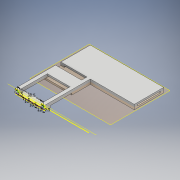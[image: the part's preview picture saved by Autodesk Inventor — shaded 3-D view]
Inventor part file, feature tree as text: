
AUTODESK INVENTOR PART (.ipt)
format: ipt  version: 2018 (Build 220112000, 112)  size: 287,232 bytes
history: native  units: mm
features: extrude x11, sketch x7, plane x3, other x2, mirror x2, projected_geometry x1
ambient origin geometry x8: Origin, YZ Plane, XZ Plane, XY Plane, X Axis, Y Axis, Z Axis, Center Point
bodies: Body1 (feature_tree)
feature tree (26):
  other  "Sólido1"
  sketch  "Boceto1"  dims[d7=5.0mm d9=2.5mm d10=0.0mm]
  extrude  "Extrusión1"  Depth=2.5mm TaperAngle=0.0deg
  extrude  "Extrusión2"  Depth=5.0mm
  plane  "Plano de trabajo3"
  mirror  "Simetría3"
  extrude  "Extrusión11"  Depth=5.0mm
  sketch  "Boceto7"  dims[d69=33.5mm d74=5.0mm]
  plane  "Plano de trabajo4"
  extrude  "Extrusión12"  Depth=5.0mm
  extrude  "Extrusión13"  Depth=8.0mm
  extrude  "Extrusión14"  Depth=42.4mm
  mirror  "Simetría4"
  extrude  "Extrusión15"  Depth=2.5mm TaperAngle=0.0deg
  sketch  "Boceto9"  dims[d77=70.0mm d78=8.0mm]
  other  "Eje de trabajo2"
  extrude  "Extrusión16"  TaperAngle=120.0deg  [1 undecoded]
  plane  "Plano de trabajo5"
  extrude  "Extrusión17"  Depth=5.0mm TaperAngle=0.0deg
  sketch  "Boceto11"  dims[d82=173.0mm d86=21.75mm d87=0.0mm d88=120.0deg d89=5.0mm d90=0.0mm d92=21.75mm d93=0.0mm d94=5.0mm d95=20.5mm d96=5.0mm d97=5.0mm d98=5.0mm d99=5.0mm d100=5.0mm d101=22.0mm d102=22.38mm d103=23.0mm d104=24.38mm d105=25.5mm d106=21.75mm d107=0.0mm d108=5.0mm d109=2.5mm d110=40.0mm d111=30.0mm d112=31.5mm d113=21.75mm d114=0.0mm d115=10.0mm d116=0.0mm d117=2.5mm d118=2.5mm d119=38.5mm d120=1.5mm d121=1.5mm d122=1.5mm d123=10.0mm d124=10.0mm d125=12.0mm d126=2.5mm d127=0.0mm d128=2.5mm d129=0.0mm]
  extrude  "Extrusión18"  Depth=2.5mm TaperAngle=0.0deg
  extrude  "Extrusión19"  Depth=5.0mm
  sketch  "Boceto6"  dims[d11=1.0mm d12=0.0mm d68=5.0mm]
  sketch  "Boceto8"  dims[d75=33.5mm d76=5.0mm]
  sketch  "Boceto10"  dims[d79=4.5mm d80=0.0mm d81=42.4mm]
  projected_geometry  "Contorno proyectado2"
note: 1 required parameter value undecoded (feature->parameter linkage not recoverable at this tier; creation-order binding heuristic only, values carry confidence <= 0.55)
